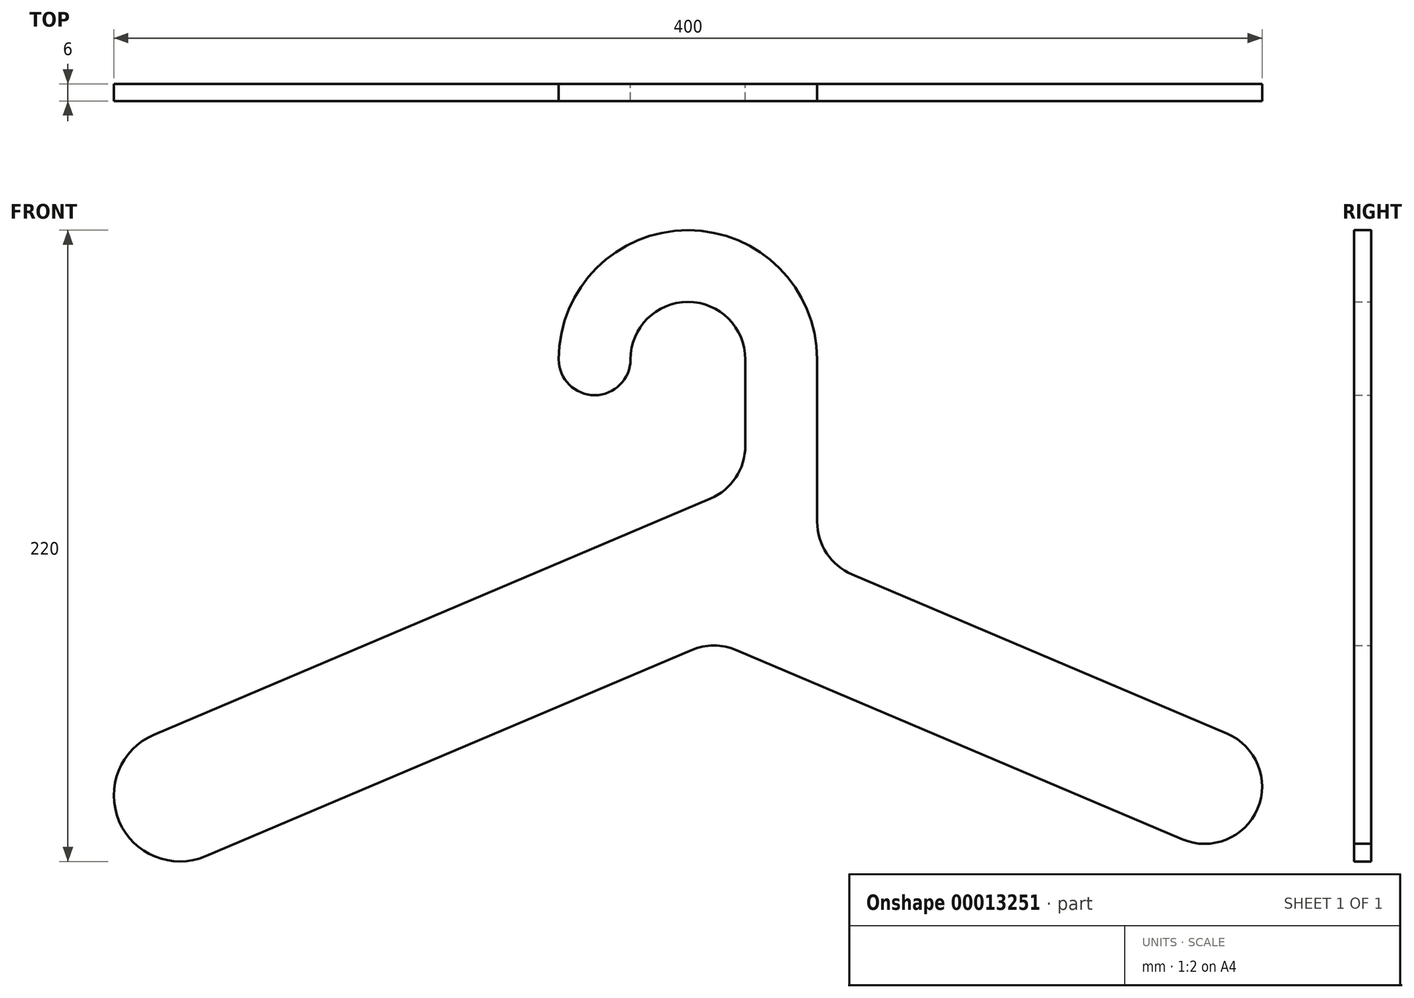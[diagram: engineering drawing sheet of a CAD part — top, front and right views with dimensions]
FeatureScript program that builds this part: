
annotation { "Feature Type Name" : "Feature", "Feature Type Description" : "" }
export const myFeature = defineFeature(function(context is Context, id is Id, definition is map)
    precondition{}
    {
        {
            var Q0;
            Q0=qCreatedBy(makeId("Front.planeOp"),FACE);
            var sketch = newSketch(context, id + "F0", { "sketchPlane" : qUnion([Q0])});
            skPoint(sketch, "E0", {"position": v(-207.11, -81) * mm});
            skLineSegment(sketch, "E1.bottom", {"start": v(-197.11, -116.73) * mm, "end": v(202.89, -116.73) * mm, "construction": true});
            skLineSegment(sketch, "E1.top", {"start": v(-197.11, 103.27) * mm, "end": v(202.89, 103.27) * mm, "construction": true});
            skLineSegment(sketch, "E1.left", {"start": v(-197.11, -116.73) * mm, "end": v(-197.11, 103.27) * mm, "construction": true});
            skLineSegment(sketch, "E1.right", {"start": v(202.89, -116.73) * mm, "end": v(202.89, 103.27) * mm, "construction": true});
            skArc(sketch, "E2.0", {"start": v(22.89, 58.27) * mm, "mid": v(2.89, 78.27) * mm, "end": v(-17.11, 58.27) * mm});
            skArc(sketch, "E3.trimOffspring", {"start": v(47.89, 58.27) * mm, "mid": v(2.89, 103.27) * mm, "end": v(-42.11, 58.27) * mm});
            skArc(sketch, "E4", {"start": v(-42.11, 58.27) * mm, "mid": v(-29.61, 45.77) * mm, "end": v(-17.11, 58.27) * mm});
            skCircle(sketch, "E5", {"center": v(-174.11, -93.73) * mm, "radius": 23 * mm});
            skLineSegment(sketch, "E6.0", {"start": v(2.89, -123.16) * mm, "end": v(2.89, 179.2) * mm, "construction": true});
            skLineSegment(sketch, "E7", {"start": v(-169.43, -116.73) * mm, "end": v(4.11, -43.07) * mm});
            skLineSegment(sketch, "E8.trimOffspring", {"start": v(-183.1, -72.56) * mm, "end": v(2.89, 6.39) * mm});
            skCircle(sketch, "E9", {"center": v(182.89, -90.6) * mm, "radius": 20 * mm});
            skPoint(sketch, "E10", {"position": v(2.89, 6.39) * mm});
            skLineSegment(sketch, "E11", {"start": v(2.89, 6.39) * mm, "end": v(10.7, 9.7) * mm});
            skLineSegment(sketch, "E12", {"start": v(11.85, -39.79) * mm, "end": v(105.25, -0.14) * mm, "construction": true});
            skLineSegment(sketch, "E13", {"start": v(19.74, -43.07) * mm, "end": v(175.07, -109) * mm});
            skLineSegment(sketch, "E14.0", {"start": v(60.07, -16.73) * mm, "end": v(191.4, -72.48) * mm});
            skLineSegment(sketch, "E15", {"start": v(47.89, 58.27) * mm, "end": v(47.89, 1.68) * mm});
            skLineSegment(sketch, "E16", {"start": v(22.89, 58.27) * mm, "end": v(22.89, 28.11) * mm});
            skArc(sketch, "E17.filletArc", {"start": v(19.74, -43.07) * mm, "mid": v(11.93, -41.48) * mm, "end": v(4.11, -43.07) * mm});
            skPoint(sketch, "E18.newPointB", {"position": v(22.89, -61.52) * mm});
            skArc(sketch, "E18.filletArc", {"start": v(10.7, 9.7) * mm, "mid": v(19.57, 17.07) * mm, "end": v(22.89, 28.11) * mm});
            skPoint(sketch, "E19.newPointA", {"position": v(47.89, -61.52) * mm});
            skArc(sketch, "E19.filletArc", {"start": v(47.89, 1.68) * mm, "mid": v(51.21, -9.36) * mm, "end": v(60.07, -16.73) * mm});
            skLineSegment(sketch, "E20", {"start": v(19.74, -43.07) * mm, "end": v(-84.88, 1.34) * mm, "construction": true});
            skLineSegment(sketch, "E21", {"start": v(60.07, -16.73) * mm, "end": v(-41.56, 26.4) * mm, "construction": true});
            skLineSegment(sketch, "E22", {"start": v(2.89, 6.39) * mm, "end": v(83.85, 40.75) * mm, "construction": true});
            skSolve(sketch);
        }
        {
            var Q0;
            {var subQ0=sQuery(id+"F0.wireOp",EDGE,"E5");var subQ2=makeQuery(id+"F0.imprint","INTERSECT",VERTEX,{"derivedFrom":[subQ0,sQuery(id+"F0.wireOp",EDGE,"E7")]});Q0=makeQuery(id+"F0.imprint","IMPRINT",FACE,{"disambiguationData":[TD([[makeQuery(id+"F0.imprint","IMPRINT",EDGE,{"disambiguationData":[TD([[subQ2,1.0]])],"derivedFrom":subQ0}),1.0]])]});}
            var Q1;
            {var subQ0=sQuery(id+"F0.wireOp",EDGE,"192e6114-3fe4-49ff-871f-eeb24d412a5f.0");var subQ3=sQuery(id+"F0.wireOp",EDGE,"e3ea16a2-a151-4e3d-8dd7-98959dfb8ed1");var subQ4=makeQuery(id+"F0.imprint","INTERSECT",VERTEX,{"derivedFrom":[subQ3,subQ0]});Q1=makeQuery(id+"F0.imprint","IMPRINT",FACE,{"disambiguationData":[TD([[makeQuery(id+"F0.imprint","IMPRINT",EDGE,{"disambiguationData":[TD([[subQ4,1.0]])],"derivedFrom":subQ3}),1.0]])]});}
            var Q2;
            {var subQ5=sQuery(id+"F0.wireOp",EDGE,"192e6114-3fe4-49ff-871f-eeb24d412a5f.0");var subQ7=sQuery(id+"F0.wireOp",EDGE,"e3ea16a2-a151-4e3d-8dd7-98959dfb8ed1");var subQ8=makeQuery(id+"F0.imprint","INTERSECT",VERTEX,{"derivedFrom":[subQ7,subQ5]});Q2=makeQuery(id+"F0.imprint","IMPRINT",FACE,{"disambiguationData":[TD([[makeQuery(id+"F0.imprint","IMPRINT",EDGE,{"disambiguationData":[TD([[subQ8,1.0]])],"derivedFrom":subQ7}),-1.0]])]});}
            var Q3;
            {var subQ6=sQuery(id+"F0.wireOp",EDGE,"E2.0");Q3=makeQuery(id+"F0.imprint","IMPRINT",FACE,{"disambiguationData":[TD([[makeQuery(id+"F0.imprint","IMPRINT",EDGE,{"derivedFrom":subQ6}),-1.0]])]});}
            var Q4;
            Q4=makeQuery(id+"F0.imprint","IMPRINT",FACE,{"disambiguationData":[TD([[makeQuery(id+"F0.imprint","IMPRINT",EDGE,{"derivedFrom":sQuery(id+"F0.wireOp",EDGE,"a17f8a86-cc57-402f-9a8f-cf5492933729")}),1.0]])]});
            var Q5;
            {var subQ1=sQuery(id+"F0.wireOp",EDGE,"E7");var subQ3=sQuery(id+"F0.wireOp",EDGE,"909c0b40-9089-425f-9131-edce53e26c64");var subQ5=makeQuery(id+"F0.imprint","INTERSECT",VERTEX,{"derivedFrom":[subQ3,subQ1]});Q5=makeQuery(id+"F0.imprint","IMPRINT",FACE,{"disambiguationData":[TD([[makeQuery(id+"F0.imprint","IMPRINT",EDGE,{"disambiguationData":[TD([[subQ5,-1.0]])],"derivedFrom":subQ3}),1.0]])]});}
            var Q6;
            {var subQ3=sQuery(id+"F0.wireOp",EDGE,"909c0b40-9089-425f-9131-edce53e26c64");var subQ5=sQuery(id+"F0.wireOp",EDGE,"d3a99e3b-3d39-4ce0-b772-3e988730ee3d");var subQ6=makeQuery(id+"F0.imprint","INTERSECT",VERTEX,{"derivedFrom":[subQ3,subQ5]});Q6=makeQuery(id+"F0.imprint","IMPRINT",FACE,{"disambiguationData":[TD([[makeQuery(id+"F0.imprint","IMPRINT",EDGE,{"disambiguationData":[TD([[subQ6,-1.0]])],"derivedFrom":subQ3}),-1.0]])]});}
            var Q7;
            {var subQ3=sQuery(id+"F0.wireOp",EDGE,"909c0b40-9089-425f-9131-edce53e26c64");var subQ5=sQuery(id+"F0.wireOp",EDGE,"25644898-7a8d-403f-a46f-4714e3b78419.0");var subQ7=makeQuery(id+"F0.imprint","INTERSECT",VERTEX,{"derivedFrom":[subQ5,subQ3]});Q7=makeQuery(id+"F0.imprint","IMPRINT",FACE,{"disambiguationData":[TD([[makeQuery(id+"F0.imprint","IMPRINT",EDGE,{"disambiguationData":[TD([[subQ7,1.0]])],"derivedFrom":subQ5}),1.0]])]});}
            var Q8;
            {var subQ1=sQuery(id+"F0.wireOp",EDGE,"192e6114-3fe4-49ff-871f-eeb24d412a5f.0");var subQ3=sQuery(id+"F0.wireOp",EDGE,"909c0b40-9089-425f-9131-edce53e26c64");var subQ5=makeQuery(id+"F0.imprint","INTERSECT",VERTEX,{"derivedFrom":[subQ3,subQ1]});Q8=makeQuery(id+"F0.imprint","IMPRINT",FACE,{"disambiguationData":[TD([[makeQuery(id+"F0.imprint","IMPRINT",EDGE,{"disambiguationData":[TD([[subQ5,1.0]])],"derivedFrom":subQ3}),-1.0]])]});}
            var Q9;
            {var subQ1=sQuery(id+"F0.wireOp",EDGE,"E8.trimOffspring");var subQ5=sQuery(id+"F0.wireOp",EDGE,"E5");var subQ6=makeQuery(id+"F0.imprint","INTERSECT",VERTEX,{"derivedFrom":[subQ5,subQ1]});Q9=makeQuery(id+"F0.imprint","IMPRINT",FACE,{"disambiguationData":[TD([[makeQuery(id+"F0.imprint","IMPRINT",EDGE,{"disambiguationData":[TD([[subQ6,1.0]])],"derivedFrom":subQ5}),-1.0]])]});}
            var Q10;
            {var subQ0=sQuery(id+"F0.wireOp",EDGE,"E14.0");var subQ3=makeQuery(id+"F0.imprint","INTERSECT",VERTEX,{"derivedFrom":[sQuery(id+"F0.wireOp",EDGE,"d3a99e3b-3d39-4ce0-b772-3e988730ee3d"),subQ0]});Q10=makeQuery(id+"F0.imprint","IMPRINT",FACE,{"disambiguationData":[TD([[makeQuery(id+"F0.imprint","IMPRINT",EDGE,{"disambiguationData":[TD([[subQ3,-1.0]])],"derivedFrom":subQ0}),-1.0]])]});}
            var Q11;
            {var subQ0=sQuery(id+"F0.wireOp",EDGE,"E14.0");var subQ3=sQuery(id+"F0.wireOp",EDGE,"d3a99e3b-3d39-4ce0-b772-3e988730ee3d");var subQ4=makeQuery(id+"F0.imprint","INTERSECT",VERTEX,{"derivedFrom":[subQ3,subQ0]});Q11=makeQuery(id+"F0.imprint","IMPRINT",FACE,{"disambiguationData":[TD([[makeQuery(id+"F0.imprint","IMPRINT",EDGE,{"disambiguationData":[TD([[subQ4,1.0]])],"derivedFrom":subQ3}),-1.0]])]});}
            var Q12;
            {var subQ3=sQuery(id+"F0.wireOp",EDGE,"E9");var subQ5=sQuery(id+"F0.wireOp",EDGE,"E13");var subQ6=makeQuery(id+"F0.imprint","INTERSECT",VERTEX,{"derivedFrom":[subQ3,subQ5]});Q12=makeQuery(id+"F0.imprint","IMPRINT",FACE,{"disambiguationData":[TD([[makeQuery(id+"F0.imprint","IMPRINT",EDGE,{"disambiguationData":[TD([[subQ6,1.0]])],"derivedFrom":subQ3}),-1.0]])]});}
            var Q13;
            {var subQ0=sQuery(id+"F0.wireOp",EDGE,"E9");var subQ2=makeQuery(id+"F0.imprint","INTERSECT",VERTEX,{"derivedFrom":[subQ0,sQuery(id+"F0.wireOp",EDGE,"E13")]});Q13=makeQuery(id+"F0.imprint","IMPRINT",FACE,{"disambiguationData":[TD([[makeQuery(id+"F0.imprint","IMPRINT",EDGE,{"disambiguationData":[TD([[subQ2,1.0]])],"derivedFrom":subQ0}),1.0]])]});}
            var Q14;
            {var subQ3=sQuery(id+"F0.wireOp",EDGE,"E11");var subQ5=sQuery(id+"F0.wireOp",EDGE,"E15");var subQ7=makeQuery(id+"F0.imprint","INTERSECT",VERTEX,{"derivedFrom":[subQ3,subQ5]});Q14=makeQuery(id+"F0.imprint","IMPRINT",FACE,{"disambiguationData":[TD([[makeQuery(id+"F0.imprint","IMPRINT",EDGE,{"disambiguationData":[TD([[subQ7,1.0]])],"derivedFrom":subQ3}),-1.0]])]});}
            var Q15;
            {var subQ0=sQuery(id+"F0.wireOp",EDGE,"E16");var subQ3=sQuery(id+"F0.wireOp",EDGE,"E11");var subQ4=makeQuery(id+"F0.imprint","INTERSECT",VERTEX,{"derivedFrom":[subQ3,subQ0]});Q15=makeQuery(id+"F0.imprint","IMPRINT",FACE,{"disambiguationData":[TD([[makeQuery(id+"F0.imprint","IMPRINT",EDGE,{"disambiguationData":[TD([[subQ4,-1.0]])],"derivedFrom":subQ0}),-1.0]])]});}
            var Q16;
            {var subQ0=sQuery(id+"F0.wireOp",EDGE,"E16");var subQ1=sQuery(id+"F0.wireOp",EDGE,"E12");var subQ2=makeQuery(id+"F0.imprint","INTERSECT",VERTEX,{"derivedFrom":[subQ1,subQ0]});Q16=makeQuery(id+"F0.imprint","IMPRINT",FACE,{"disambiguationData":[TD([[makeQuery(id+"F0.imprint","IMPRINT",EDGE,{"disambiguationData":[TD([[subQ2,-1.0]])],"derivedFrom":subQ1}),-1.0]])]});}
            var Q17;
            {var subQ0=sQuery(id+"F0.wireOp",EDGE,"E16");var subQ3=sQuery(id+"F0.wireOp",EDGE,"E12");var subQ4=makeQuery(id+"F0.imprint","INTERSECT",VERTEX,{"derivedFrom":[subQ3,subQ0]});Q17=makeQuery(id+"F0.imprint","IMPRINT",FACE,{"disambiguationData":[TD([[makeQuery(id+"F0.imprint","IMPRINT",EDGE,{"disambiguationData":[TD([[subQ4,-1.0]])],"derivedFrom":subQ3}),1.0]])]});}
            var Q18;
            {var subQ0=sQuery(id+"F0.wireOp",EDGE,"E16");var subQ3=sQuery(id+"F0.wireOp",EDGE,"E12");var subQ4=makeQuery(id+"F0.imprint","INTERSECT",VERTEX,{"derivedFrom":[subQ3,subQ0]});Q18=makeQuery(id+"F0.imprint","IMPRINT",FACE,{"disambiguationData":[TD([[makeQuery(id+"F0.imprint","IMPRINT",EDGE,{"disambiguationData":[TD([[subQ4,1.0]])],"derivedFrom":subQ0}),-1.0]])]});}
            var Q19;
            {var subQ0=sQuery(id+"F0.wireOp",EDGE,"E16");var subQ3=sQuery(id+"F0.wireOp",EDGE,"E13");var subQ4=makeQuery(id+"F0.imprint","INTERSECT",VERTEX,{"derivedFrom":[subQ3,subQ0]});Q19=makeQuery(id+"F0.imprint","IMPRINT",FACE,{"disambiguationData":[TD([[makeQuery(id+"F0.imprint","IMPRINT",EDGE,{"disambiguationData":[TD([[subQ4,1.0]])],"derivedFrom":subQ0}),-1.0]])]});}
            extrude(context, id + "F1", {"entities" : qUnion([Q0, Q1, Q2, Q3, Q4, Q5, Q6, Q7, Q8, Q9, Q10, Q11, Q12, Q13, Q14, Q15, Q16, Q17, Q18, Q19]), "depth" : 6 * mm});
        }
    });
